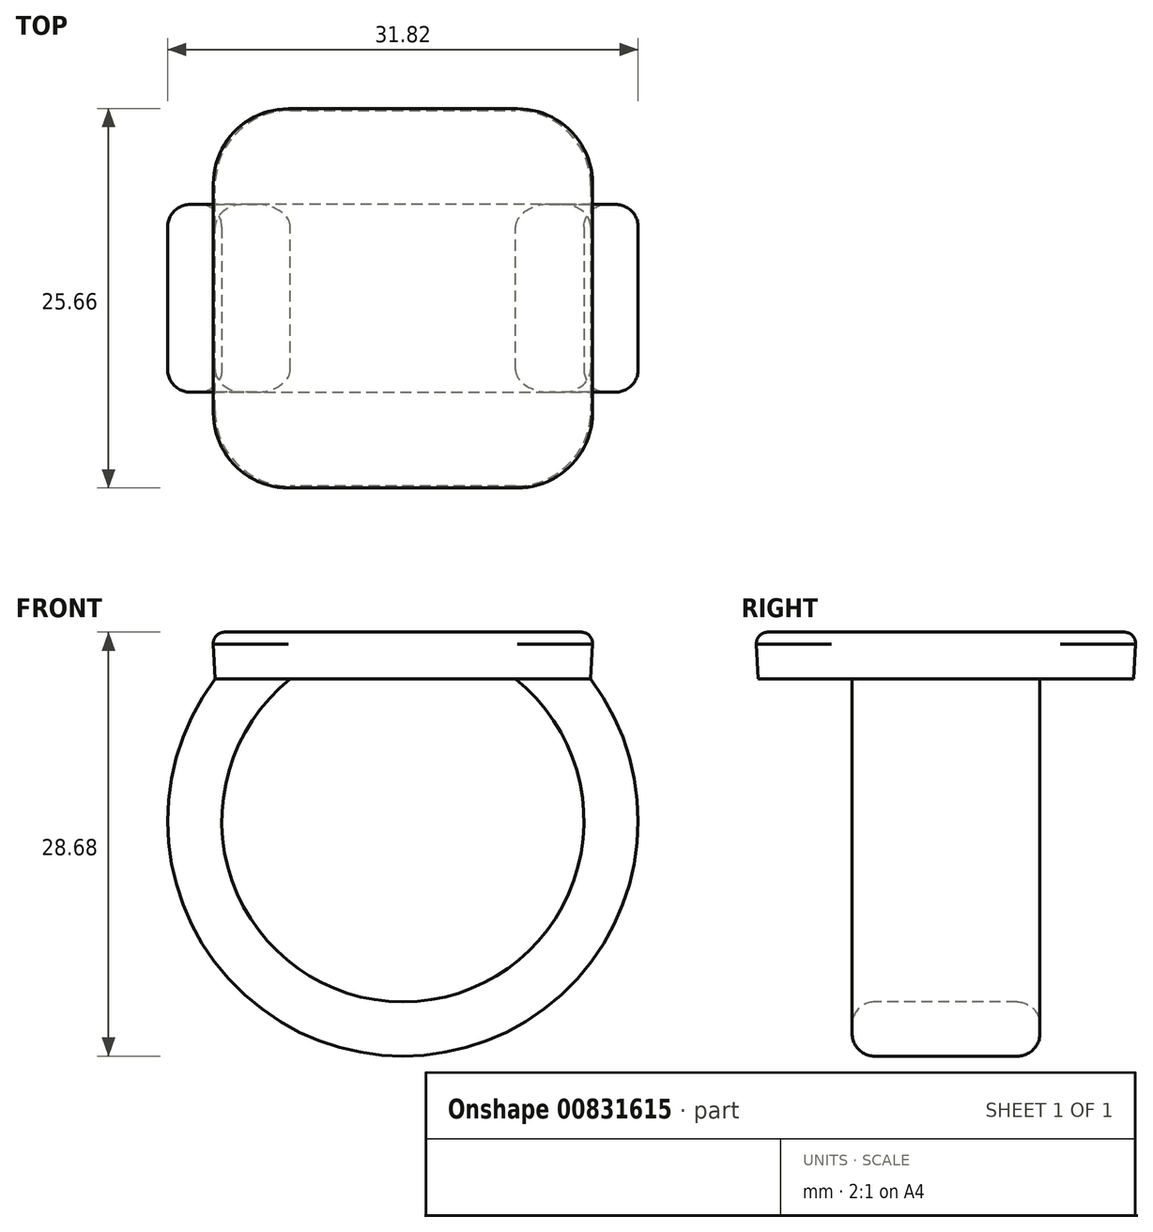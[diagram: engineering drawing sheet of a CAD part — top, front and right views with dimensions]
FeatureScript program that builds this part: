
annotation { "Feature Type Name" : "Feature", "Feature Type Description" : "" }
export const myFeature = defineFeature(function(context is Context, id is Id, definition is map)
    precondition{}
    {
        {
            var Q0;
            Q0=qCreatedBy(makeId("Top.planeOp"),FACE);
            var sketch = newSketch(context, id + "F0", { "sketchPlane" : qUnion([Q0])});
            skLineSegment(sketch, "E0.bottom", {"start": v(12.7, -12.7) * mm, "end": v(-12.7, -12.7) * mm});
            skLineSegment(sketch, "E0.top", {"start": v(12.7, 12.7) * mm, "end": v(-12.7, 12.7) * mm});
            skLineSegment(sketch, "E0.left", {"start": v(12.7, -12.7) * mm, "end": v(12.7, 12.7) * mm});
            skLineSegment(sketch, "E0.right", {"start": v(-12.7, -12.7) * mm, "end": v(-12.7, 12.7) * mm});
            skPoint(sketch, "E0.middle", {"position": v(0, 0) * mm});
            skSolve(sketch);
        }
        {
            var Q0;
            Q0=qSketchRegion(id+"F0",true);
            extrude(context, id + "F1", {"entities" : qUnion([Q0]), "depth" : 3.17 * mm, "offsetDistance" : 25.4 * mm, "hasDraft" : true, "draftAngle" : 3 * degree});
        }
        {
            var Q0;
            Q0=qCreatedBy(makeId("Front.planeOp"),FACE);
            var sketch = newSketch(context, id + "F2", { "sketchPlane" : qUnion([Q0])});
            skArc(sketch, "E1", {"start": v(-10.16, 0) * mm, "mid": v(0, -23.56) * mm, "end": v(10.16, 0) * mm});
            skSolve(sketch);
        }
        {
            var Q0;
            Q0=makeQuery(id+"F1.opExtrude","CAP_FACE",FACE,{"disambiguationData":[OSD([sQuery(id+"F0.wireOp",EDGE,"E0.bottom"),sQuery(id+"F0.wireOp",EDGE,"E0.top"),sQuery(id+"F0.wireOp",EDGE,"E0.left"),sQuery(id+"F0.wireOp",EDGE,"E0.right")])],"isStart":true});
            var sketch = newSketch(context, id + "F3", { "sketchPlane" : qUnion([Q0])});
            skLineSegment(sketch, "E2.bottom", {"start": v(-7.62, 6.35) * mm, "end": v(-12.7, 6.35) * mm});
            skLineSegment(sketch, "E2.top", {"start": v(-7.62, -6.35) * mm, "end": v(-12.7, -6.35) * mm});
            skLineSegment(sketch, "E2.left", {"start": v(-7.62, 6.35) * mm, "end": v(-7.62, -6.35) * mm});
            skLineSegment(sketch, "E2.right", {"start": v(-12.7, 6.35) * mm, "end": v(-12.7, -6.35) * mm});
            skPoint(sketch, "E2.middle", {"position": v(-10.16, 0) * mm});
            skSolve(sketch);
        }
        {
            var Q0;
            Q0=qSketchRegion(id+"F3",true);
            var Q1;
            Q1=qConstructionFilter(qBodyType(qCreatedBy(id+"F2",EDGE),BodyType.WIRE),ConstructionObject.NO);
            sweep(context, id + "F4", {"operationType" : NewBodyOperationType.ADD, "profiles" : qUnion([Q0]), "path" : qUnion([Q1])});
        }
        {
            var Q0;
            Q0=qCreatedBy(makeId("Front.planeOp"),FACE);
            var sketch = newSketch(context, id + "F5", { "sketchPlane" : qUnion([Q0])});
            skLineSegment(sketch, "E3.0", {"start": v(10.16, 0) * mm, "end": v(7.62, 0) * mm});
            skArc(sketch, "E3.1", {"start": v(10.01, -2.54) * mm, "mid": v(8.9, -1.18) * mm, "end": v(7.62, 0) * mm});
            skLineSegment(sketch, "E3.2", {"start": v(10.01, -2.54) * mm, "end": v(10.16, 0) * mm});
            skPoint(sketch, "E4.orphan", {"position": v(10.01, -2.54) * mm});
            skPoint(sketch, "E5.orphan", {"position": v(-12.7, 0) * mm});
            skPoint(sketch, "E6.orphan", {"position": v(12.7, 0) * mm});
            skPoint(sketch, "E7.orphan", {"position": v(-7.62, 0) * mm});
            skSolve(sketch);
        }
        {
            var Q0;
            Q0=makeQuery(id+"F5.imprint","IMPRINT",FACE,{"disambiguationData":[TD([[makeQuery(id+"F5.imprint","IMPRINT",EDGE,{"derivedFrom":sQuery(id+"F5.wireOp",EDGE,"E3.0")}),1.0]])]});
            var Q1;
            Q1=makeQuery(id+"F4.opSweep","SWEPT_FACE",FACE,{"disambiguationData":[OSD([sQuery(id+"F2.wireOp",EDGE,"E1"),sQuery(id+"F3.wireOp",EDGE,"E2.bottom")])]});
            var Q2;
            Q2=makeQuery(id+"F4.opSweep","SWEPT_FACE",FACE,{"disambiguationData":[OSD([sQuery(id+"F2.wireOp",EDGE,"E1"),sQuery(id+"F3.wireOp",EDGE,"E2.top")])]});
            extrude(context, id + "F6", {"entities" : qUnion([Q0]), "operationType" : NewBodyOperationType.ADD, "endBound" : BoundingType.UP_TO_SURFACE, "depth" : 25.4 * mm, "endBoundEntityFace" : qUnion([Q1]), "offsetDistance" : 25.4 * mm, "hasSecondDirection" : true, "secondDirectionBound" : SecondDirectionBoundingType.UP_TO_SURFACE, "secondDirectionOppositeDirection" : true, "secondDirectionDepth" : 25.4 * mm, "secondDirectionBoundEntityFace" : qUnion([Q2])});
        }
        {
            var Q0;
            Q0=makeQuery(id+"F1.opExtrude","SWEPT_EDGE",EDGE,{"disambiguationData":[OSD([sQuery(id+"F0.wireOp",EDGE,"E0.bottom"),sQuery(id+"F0.wireOp",EDGE,"E0.left")])]});
            var Q1;
            Q1=makeQuery(id+"F1.opExtrude","SWEPT_EDGE",EDGE,{"disambiguationData":[OSD([sQuery(id+"F0.wireOp",EDGE,"E0.top"),sQuery(id+"F0.wireOp",EDGE,"E0.left")])]});
            var Q2;
            Q2=makeQuery(id+"F1.opExtrude","SWEPT_EDGE",EDGE,{"disambiguationData":[OSD([sQuery(id+"F0.wireOp",EDGE,"E0.top"),sQuery(id+"F0.wireOp",EDGE,"E0.right")])]});
            var Q3;
            Q3=makeQuery(id+"F1.opExtrude","SWEPT_EDGE",EDGE,{"disambiguationData":[OSD([sQuery(id+"F0.wireOp",EDGE,"E0.bottom"),sQuery(id+"F0.wireOp",EDGE,"E0.right")])]});
            fillet(context, id + "F7", {"entities" : qUnion([Q0, Q1, Q2, Q3]), "radius" : 5.08 * mm, "tangentPropagation" : true, "allowEdgeOverflow" : false});
        }
        {
            var Q0;
            Q0=makeQuery(id+"F4.opSweep","SWEPT_EDGE",EDGE,{"disambiguationData":[OSD([sQuery(id+"F0.wireOp",EDGE,"E0.right"),sQuery(id+"F2.wireOp",EDGE,"E1"),sQuery(id+"F3.wireOp",EDGE,"E2.bottom"),sQuery(id+"F3.wireOp",EDGE,"E2.right")])]});
            var Q1;
            Q1=makeQuery(id+"F4.opSweep","SWEPT_EDGE",EDGE,{"disambiguationData":[OSD([sQuery(id+"F0.wireOp",EDGE,"E0.right"),sQuery(id+"F2.wireOp",EDGE,"E1"),sQuery(id+"F3.wireOp",EDGE,"E2.top"),sQuery(id+"F3.wireOp",EDGE,"E2.right")])]});
            var Q2;
            {var subQ0=sQuery(id+"F3.wireOp",EDGE,"E2.top");var subQ1=sQuery(id+"F2.wireOp",EDGE,"E1");Q2=makeQuery(id+"F6.boolean.opBoolean","MERGE",EDGE,{"derivedFrom":[makeQuery(id+"F4.opSweep","SWEPT_EDGE",EDGE,{"disambiguationData":[OSD([subQ1,subQ0,sQuery(id+"F3.wireOp",EDGE,"E2.left")])]}),makeQuery(id+"F6.opExtrude","TWEAK_EDGE",EDGE,{"derivedFrom":[makeQuery(id+"F4.opSweep","SWEPT_FACE",FACE,{"disambiguationData":[OSD([subQ1,subQ0])]}),makeQuery(id+"F5.imprint","IMPRINT",EDGE,{"derivedFrom":sQuery(id+"F5.wireOp",EDGE,"E3.1")})]})]});}
            var Q3;
            {var subQ0=sQuery(id+"F3.wireOp",EDGE,"E2.bottom");var subQ1=sQuery(id+"F2.wireOp",EDGE,"E1");Q3=makeQuery(id+"F6.boolean.opBoolean","MERGE",EDGE,{"derivedFrom":[makeQuery(id+"F4.opSweep","SWEPT_EDGE",EDGE,{"disambiguationData":[OSD([subQ1,subQ0,sQuery(id+"F3.wireOp",EDGE,"E2.left")])]}),makeQuery(id+"F6.opExtrude","TWEAK_EDGE",EDGE,{"derivedFrom":[makeQuery(id+"F4.opSweep","SWEPT_FACE",FACE,{"disambiguationData":[OSD([subQ1,subQ0])]}),makeQuery(id+"F5.imprint","IMPRINT",EDGE,{"derivedFrom":sQuery(id+"F5.wireOp",EDGE,"E3.1")})]})]});}
            fillet(context, id + "F8", {"entities" : qUnion([Q0, Q1, Q2, Q3]), "radius" : 1.52 * mm, "tangentPropagation" : true, "allowEdgeOverflow" : false});
        }
        {
            var Q0;
            Q0=makeQuery(id+"F1.opExtrude","CAP_FACE",FACE,{"disambiguationData":[OSD([sQuery(id+"F0.wireOp",EDGE,"E0.bottom"),sQuery(id+"F0.wireOp",EDGE,"E0.top"),sQuery(id+"F0.wireOp",EDGE,"E0.left"),sQuery(id+"F0.wireOp",EDGE,"E0.right")])],"isStart":false});
            fillet(context, id + "F9", {"entities" : qUnion([Q0]), "radius" : 0.76 * mm, "tangentPropagation" : true, "allowEdgeOverflow" : false});
        }
    });
